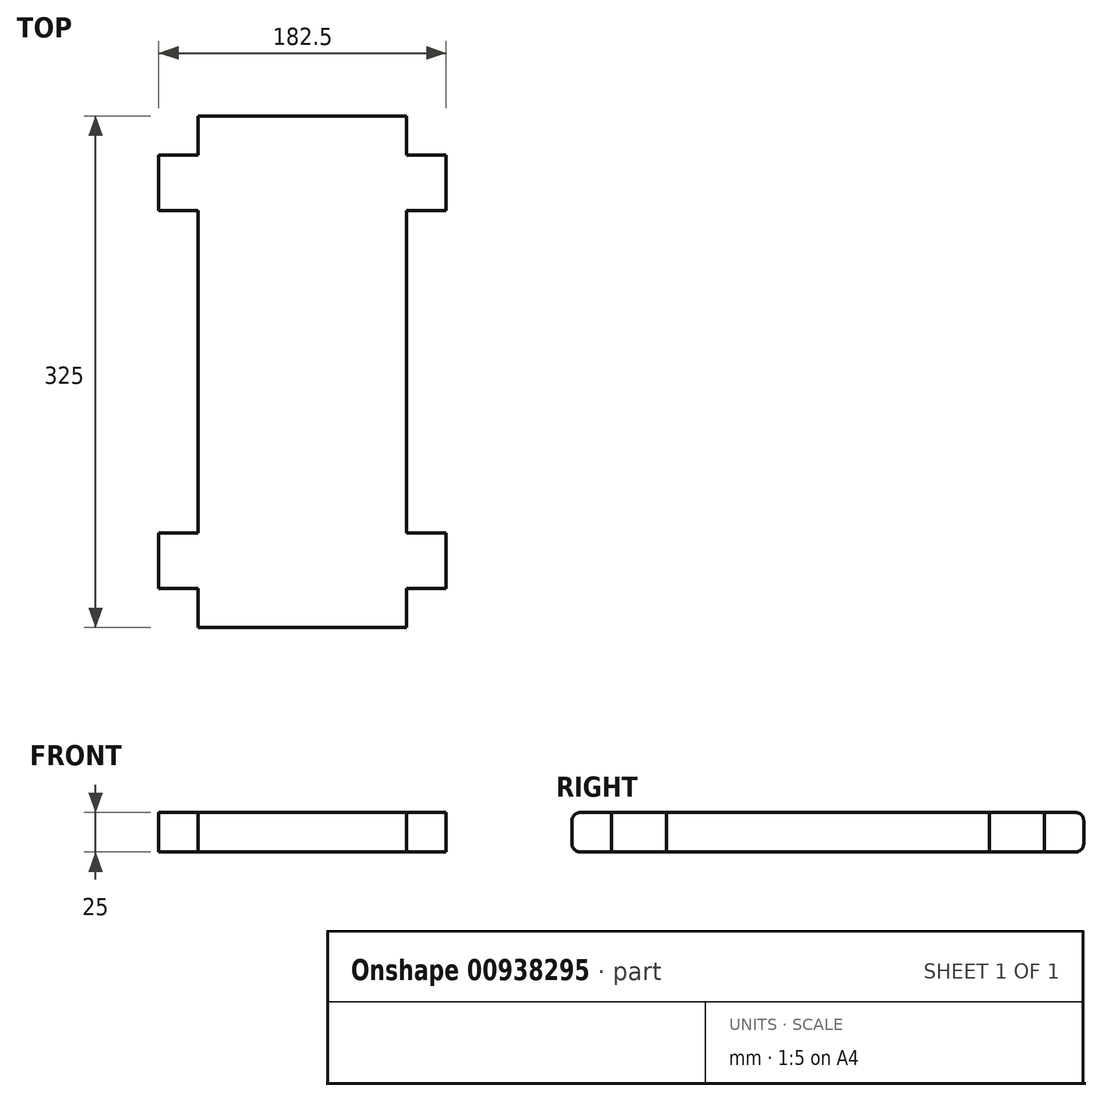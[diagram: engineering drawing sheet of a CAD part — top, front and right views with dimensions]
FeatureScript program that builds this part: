
annotation { "Feature Type Name" : "Feature", "Feature Type Description" : "" }
export const myFeature = defineFeature(function(context is Context, id is Id, definition is map)
    precondition{}
    {
        {
            var Q0;
            Q0=qCreatedBy(makeId("Top.planeOp"),FACE);
            var sketch = newSketch(context, id + "F0", { "sketchPlane" : qUnion([Q0])});
            skLineSegment(sketch, "E0.bottom", {"start": v(-68.7, 256.63) * mm, "end": v(-2.45, 256.63) * mm});
            skLineSegment(sketch, "E0.top", {"start": v(-68.7, -68.37) * mm, "end": v(-2.45, -68.37) * mm});
            skLineSegment(sketch, "E0.left", {"start": v(-68.7, 256.63) * mm, "end": v(-68.7, -68.37) * mm});
            skLineSegment(sketch, "E0.right", {"start": v(-2.45, 256.63) * mm, "end": v(-2.45, -68.37) * mm});
            skLineSegment(sketch, "E1.bottom", {"start": v(-68.7, -43.37) * mm, "end": v(-93.7, -43.37) * mm});
            skLineSegment(sketch, "E1.top", {"start": v(-68.7, -8.37) * mm, "end": v(-93.7, -8.37) * mm});
            skLineSegment(sketch, "E1.left", {"start": v(-68.7, -43.37) * mm, "end": v(-68.7, -8.37) * mm});
            skLineSegment(sketch, "E1.right", {"start": v(-93.7, -43.37) * mm, "end": v(-93.7, -8.37) * mm});
            skLineSegment(sketch, "E2.bottom", {"start": v(-68.7, 196.63) * mm, "end": v(-93.7, 196.63) * mm});
            skLineSegment(sketch, "E2.top", {"start": v(-68.7, 231.63) * mm, "end": v(-93.7, 231.63) * mm});
            skLineSegment(sketch, "E2.left", {"start": v(-68.7, 196.63) * mm, "end": v(-68.7, 231.63) * mm});
            skLineSegment(sketch, "E2.right", {"start": v(-93.7, 196.63) * mm, "end": v(-93.7, 231.63) * mm});
            skSolve(sketch);
        }
        {
            var Q0;
            {var subQ0=sQuery(id+"F0.wireOp",EDGE,"E1.bottom");var subQ6=sQuery(id+"F0.wireOp",EDGE,"E2.bottom");var subQ9=sQuery(id+"F0.wireOp",EDGE,"E0.bottom");Q0=qUnion([makeQuery(id+"F0.imprint","IMPRINT",FACE,{"disambiguationData":[TD([[makeQuery(id+"F0.imprint","IMPRINT",EDGE,{"derivedFrom":subQ0}),-1.0]])]}),makeQuery(id+"F0.imprint","IMPRINT",FACE,{"disambiguationData":[TD([[makeQuery(id+"F0.imprint","IMPRINT",EDGE,{"derivedFrom":subQ6}),-1.0]])]}),makeQuery(id+"F0.imprint","IMPRINT",FACE,{"disambiguationData":[TD([[makeQuery(id+"F0.imprint","IMPRINT",EDGE,{"derivedFrom":subQ9}),-1.0]])]})]);}
            extrude(context, id + "F1", {"entities" : qUnion([Q0]), "depth" : 25 * mm, "offsetDistance" : 25 * mm});
        }
        {
            var Q0;
            Q0=makeQuery(id+"F1.opExtrude","SWEPT_BODY",BODY,{"disambiguationData":[OSD([sQuery(id+"F0.wireOp",EDGE,"E0.bottom"),sQuery(id+"F0.wireOp",EDGE,"E0.top"),sQuery(id+"F0.wireOp",EDGE,"E0.left"),sQuery(id+"F0.wireOp",EDGE,"E0.right"),sQuery(id+"F0.wireOp",EDGE,"E1.bottom"),sQuery(id+"F0.wireOp",EDGE,"E1.top"),sQuery(id+"F0.wireOp",EDGE,"E1.right"),sQuery(id+"F0.wireOp",EDGE,"E2.bottom"),sQuery(id+"F0.wireOp",EDGE,"E2.top"),sQuery(id+"F0.wireOp",EDGE,"E2.right")])]});
            var Q1;
            Q1=makeQuery(id+"F1.opExtrude","SWEPT_FACE",FACE,{"disambiguationData":[OSD([sQuery(id+"F0.wireOp",EDGE,"E0.right")])]});
            mirror(context, id + "F2", {"operationType" : NewBodyOperationType.ADD, "entities" : qUnion([Q0]), "mirrorPlane" : qUnion([Q1])});
        }
        {
            var Q0;
            {var subQ0=makeQuery(id+"F1.opExtrude","CAP_EDGE",EDGE,{"disambiguationData":[OSD([sQuery(id+"F0.wireOp",EDGE,"E0.bottom")])],"isStart":true});Q0=makeQuery(id+"F2.boolean.opBoolean","MERGE",EDGE,{"derivedFrom":[subQ0,makeQuery(id+"F2.opPattern","COPY",EDGE,{"derivedFrom":subQ0,"instanceName":"1"})]});}
            var Q1;
            {var subQ0=makeQuery(id+"F1.opExtrude","CAP_EDGE",EDGE,{"disambiguationData":[OSD([sQuery(id+"F0.wireOp",EDGE,"E0.bottom")])],"isStart":false});Q1=makeQuery(id+"F2.boolean.opBoolean","MERGE",EDGE,{"derivedFrom":[subQ0,makeQuery(id+"F2.opPattern","COPY",EDGE,{"derivedFrom":subQ0,"instanceName":"1"})]});}
            var Q2;
            {var subQ0=makeQuery(id+"F1.opExtrude","CAP_EDGE",EDGE,{"disambiguationData":[OSD([sQuery(id+"F0.wireOp",EDGE,"E0.top")])],"isStart":true});Q2=makeQuery(id+"F2.boolean.opBoolean","MERGE",EDGE,{"derivedFrom":[subQ0,makeQuery(id+"F2.opPattern","COPY",EDGE,{"derivedFrom":subQ0,"instanceName":"1"})]});}
            var Q3;
            {var subQ0=makeQuery(id+"F1.opExtrude","CAP_EDGE",EDGE,{"disambiguationData":[OSD([sQuery(id+"F0.wireOp",EDGE,"E0.top")])],"isStart":false});Q3=makeQuery(id+"F2.boolean.opBoolean","MERGE",EDGE,{"derivedFrom":[subQ0,makeQuery(id+"F2.opPattern","COPY",EDGE,{"derivedFrom":subQ0,"instanceName":"1"})]});}
            fillet(context, id + "F3", {"entities" : qUnion([Q0, Q1, Q2, Q3]), "radius" : 5 * mm, "tangentPropagation" : true, "allowEdgeOverflow" : false});
        }
    });
